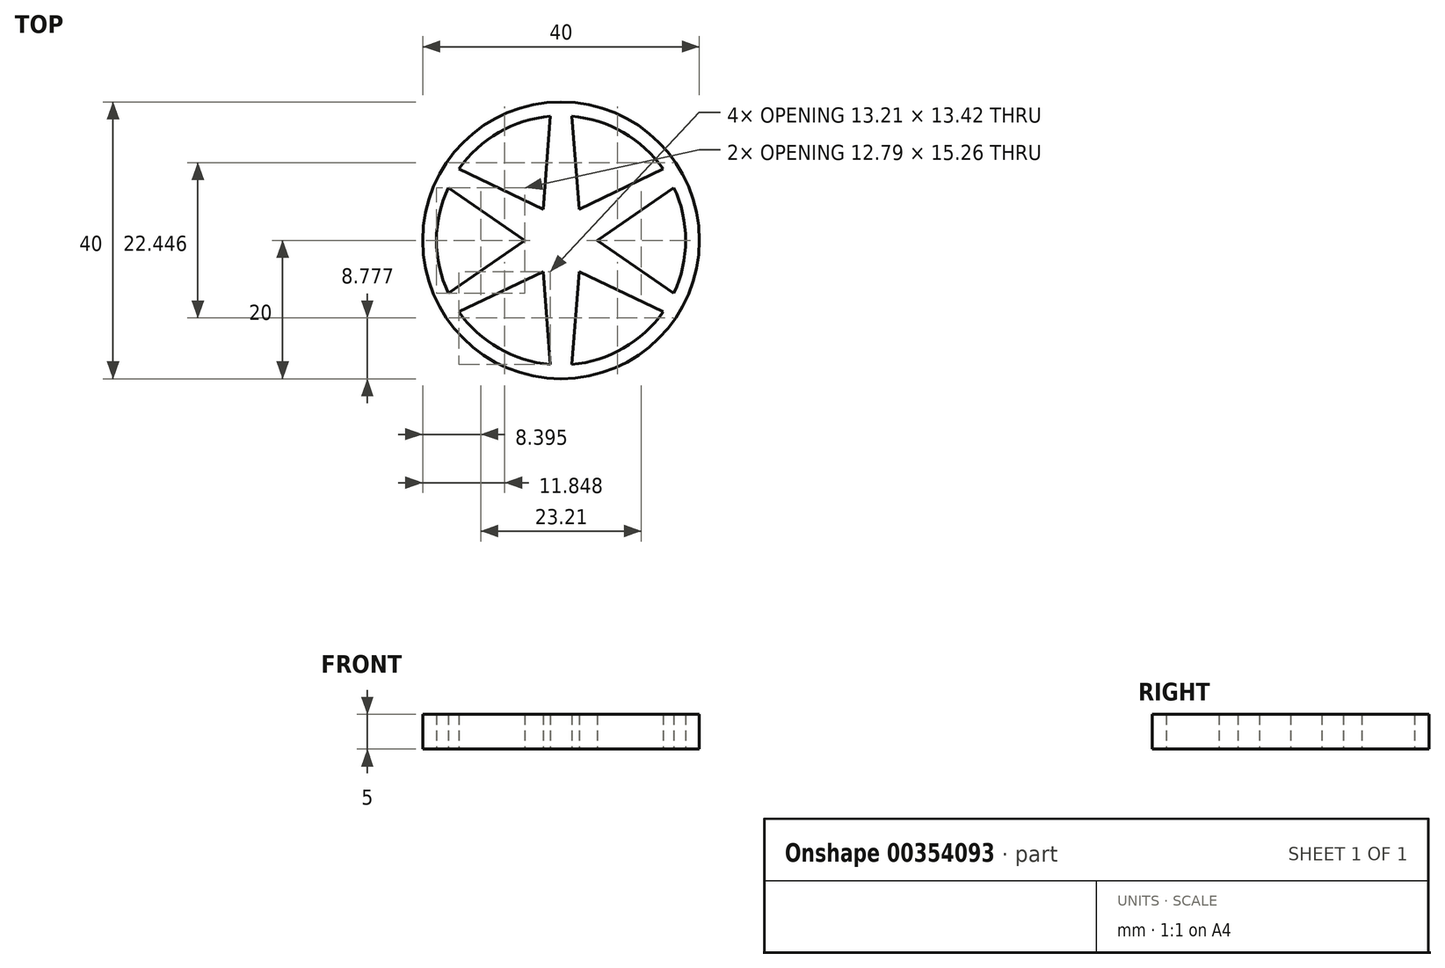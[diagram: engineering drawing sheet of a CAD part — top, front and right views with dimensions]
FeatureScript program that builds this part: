
annotation { "Feature Type Name" : "Feature", "Feature Type Description" : "" }
export const myFeature = defineFeature(function(context is Context, id is Id, definition is map)
    precondition{}
    {
        {
            var Q0;
            Q0=qCreatedBy(makeId("Top.planeOp"),FACE);
            var sketch = newSketch(context, id + "F0", { "sketchPlane" : qUnion([Q0])});
            skCircle(sketch, "E0", {"center": v(0, 0) * mm, "radius": 20 * mm});
            skArc(sketch, "E1", {"start": v(-1.55, 17.93) * mm, "mid": v(-9, 15.59) * mm, "end": v(-14.76, 10.3) * mm});
            skLineSegment(sketch, "E2", {"start": v(-2.6, 4.51) * mm, "end": v(-1.55, 17.93) * mm});
            skLineSegment(sketch, "E3.MirrorCS", {"start": v(2.6, 4.51) * mm, "end": v(1.55, 17.93) * mm});
            skLineSegment(sketch, "E4.1.0", {"start": v(-2.6, 4.51) * mm, "end": v(-14.76, 10.3) * mm});
            skLineSegment(sketch, "E4.1.1", {"start": v(-5.21, 0) * mm, "end": v(-16.3, 7.63) * mm});
            skLineSegment(sketch, "E4.2.0", {"start": v(-5.21, 0) * mm, "end": v(-16.3, -7.63) * mm});
            skLineSegment(sketch, "E4.2.1", {"start": v(-2.6, -4.51) * mm, "end": v(-14.76, -10.3) * mm});
            skLineSegment(sketch, "E4.3.0", {"start": v(-2.6, -4.51) * mm, "end": v(-1.55, -17.93) * mm});
            skLineSegment(sketch, "E4.3.1", {"start": v(2.6, -4.51) * mm, "end": v(1.55, -17.93) * mm});
            skLineSegment(sketch, "E4.4.0", {"start": v(2.6, -4.51) * mm, "end": v(14.76, -10.3) * mm});
            skLineSegment(sketch, "E4.4.1", {"start": v(5.21, 0) * mm, "end": v(16.3, -7.63) * mm});
            skLineSegment(sketch, "E4.5.0", {"start": v(5.21, 0) * mm, "end": v(16.3, 7.63) * mm});
            skLineSegment(sketch, "E4.5.1", {"start": v(2.6, 4.51) * mm, "end": v(14.76, 10.3) * mm});
            skPoint(sketch, "E5.orphan", {"position": v(-0.43, 3.47) * mm});
            skPoint(sketch, "E6.orphan", {"position": v(0.43, 3.47) * mm});
            skPoint(sketch, "E7.orphan", {"position": v(2.8, 2.1) * mm});
            skPoint(sketch, "E8.orphan", {"position": v(-2.8, 2.1) * mm});
            skPoint(sketch, "E9.orphan", {"position": v(-3.22, -1.37) * mm});
            skPoint(sketch, "E10.orphan", {"position": v(-2.8, -2.1) * mm});
            skPoint(sketch, "E11.orphan", {"position": v(3.22, -1.37) * mm});
            skArc(sketch, "E12.trimOffspring", {"start": v(-16.3, 7.63) * mm, "mid": v(-18, 0) * mm, "end": v(-16.3, -7.63) * mm});
            skArc(sketch, "E13.trimOffspring", {"start": v(-14.76, -10.3) * mm, "mid": v(-9, -15.59) * mm, "end": v(-1.55, -17.93) * mm});
            skArc(sketch, "E14.trimOffspring", {"start": v(1.55, -17.93) * mm, "mid": v(9, -15.59) * mm, "end": v(14.76, -10.3) * mm});
            skArc(sketch, "E15.trimOffspring", {"start": v(16.3, -7.63) * mm, "mid": v(18, 0) * mm, "end": v(16.3, 7.63) * mm});
            skArc(sketch, "E16.trimOffspring", {"start": v(14.76, 10.3) * mm, "mid": v(9, 15.59) * mm, "end": v(1.55, 17.93) * mm});
            skSolve(sketch);
        }
        {
            var Q0;
            Q0=makeQuery(id+"F0.imprint","IMPRINT",FACE,{"disambiguationData":[TD([[makeQuery(id+"F0.imprint","IMPRINT",EDGE,{"derivedFrom":sQuery(id+"F0.wireOp",EDGE,"E0")}),1.0]])]});
            extrude(context, id + "F1", {"entities" : qUnion([Q0]), "depth" : 5 * mm});
        }
    });
